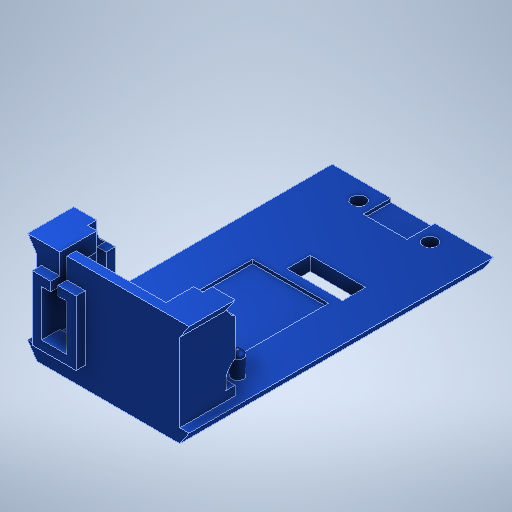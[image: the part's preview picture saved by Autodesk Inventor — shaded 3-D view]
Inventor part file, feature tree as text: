
AUTODESK INVENTOR PART (.ipt)
format: ipt  version: 2025.1 (Build 291241020, 241B)  size: 606,720 bytes
history: native  units: in
note: dims shown in document units (in); Inventor stores cm internally (conversion verified against a paired STEP export)
features: extrude x18, sketch x18, projected_geometry x15, fillet x3, mirror x2, plane x1
ambient origin geometry x8: Origin, YZ Plane, XZ Plane, XY Plane, X Axis, Y Axis, Z Axis, Center Point
bodies: Solid1 (feature_tree)
feature tree (57):
  extrude  "Extrusion1"  Depth=2.3622in
  extrude  "Extrusion2"  Depth=0.6496in
  extrude  "Extrusion7"  Depth=0.2362in
  extrude  "Extrusion8"  Depth=0.0315in TaperAngle=0.0deg
  extrude  "Extrusion9"  Depth=0.4724in
  extrude  "Extrusion13"  Depth=0.2756in
  extrude  "Extrusion14"  Depth=0.3937in TaperAngle=0.0deg
  extrude  "Extrusion15"  Depth=0.0787in
  extrude  "Extrusion16"  Depth=0.9843in
  extrude  "Extrusion17"  Depth=0.0787in
  extrude  "Extrusion18"  Depth=0.7874in TaperAngle=0.0deg
  extrude  "Extrusion19"  Depth=0.0787in TaperAngle=0.0deg
  plane  "Work Plane1"
  mirror  "Mirror1"
  extrude  "Extrusion20"  Depth=0.3937in
  fillet  "Fillet1"  Radius=0.1181in
  extrude  "Extrusion21"  Depth=0.0787in TaperAngle=0.0deg
  mirror  "Mirror2"
  extrude  "Extrusion22"  Depth=0.0787in TaperAngle=0.0deg
  extrude  "Extrusion23"  Depth=0.315in
  fillet  "Fillet2"  Radius=0.0787in
  extrude  "Extrusion24"  Depth=0.0787in TaperAngle=0.0deg
  extrude  "Extrusion25"  Depth=0.1181in
  fillet  "Fillet3"  Radius=0.1575in
  sketch  "Sketch1"  dims[d0=1.2205in d1=2.3622in]
  sketch  "Sketch2"  dims[d2=0.1181in d3=0.0in d4=0.6496in]
  projected_geometry  "Projected Loop1"
  sketch  "Sketch10"  dims[d5=0.748in d8=0.2362in]
  sketch  "Sketch11"  dims[d9=0.374in d10=0.0315in d11=0.0in]
  projected_geometry  "Projected Loop5"
  sketch  "Sketch12"  dims[d32=1.5551in d36=0.4724in]
  projected_geometry  "Projected Loop6"
  sketch  "Sketch17"  dims[d37=0.1969in d38=0.2756in]
  projected_geometry  "Projected Loop15"
  sketch  "Sketch18"  dims[d39=0.0394in d40=0.3937in d41=0.0in]
  projected_geometry  "Projected Loop16"
  sketch  "Sketch19"  dims[d42=0.3346in d43=0.0787in]
  projected_geometry  "Projected Loop17"
  sketch  "Sketch20"  dims[d44=0.0787in d45=0.0in d46=0.9843in]
  sketch  "Sketch21"  dims[d47=0.0394in d48=0.0in d57=0.0787in]
  sketch  "Sketch22"  dims[d58=0.3937in d59=0.0in d60=0.7874in d61=0.0in]
  projected_geometry  "Projected Loop18"
  sketch  "Sketch24"  dims[d62=0.1575in d63=0.0in d64=0.0787in d65=0.0in]
  sketch  "Sketch25"  dims[d66=0.2165in d67=0.3937in d68=0.1181in]
  projected_geometry  "Projected Loop19"
  sketch  "Sketch26"  dims[d69=0.2559in d70=0.0787in d71=0.0in]
  projected_geometry  "Projected Loop20"
  projected_geometry  "Projected Loop21"
  sketch  "Sketch27"  dims[d72=0.0787in d73=0.0787in d74=0.0in]
  projected_geometry  "Projected Loop22"
  sketch  "Sketch28"  dims[d75=0.0787in d76=0.315in d77=0.0787in d78=0.0in]
  projected_geometry  "Projected Loop23"
  projected_geometry  "Projected Loop24"
  sketch  "Sketch29"  dims[d79=0.0591in d80=0.0787in d81=0.0in]
  projected_geometry  "Projected Loop25"
  sketch  "Sketch30"  dims[d82=0.1412in d84=0.1181in d85=0.1575in d86=0.3937in d87=0.0in d88=0.1181in d89=0.1181in d90=0.1575in d91=0.1181in d92=0.0315in d93=0.0in d94=0.0984in d95=0.1772in d97=0.1476in d98=0.1969in d99=0.0in d100=0.0433in d101=0.1476in d102=0.0787in d103=0.0787in d104=0.1969in d105=0.0in d106=0.0787in d108=0.0787in d110=0.1181in d111=0.1181in d112=0.3937in d113=0.0in d117=0.0787in]
  projected_geometry  "Projected Loop26"
